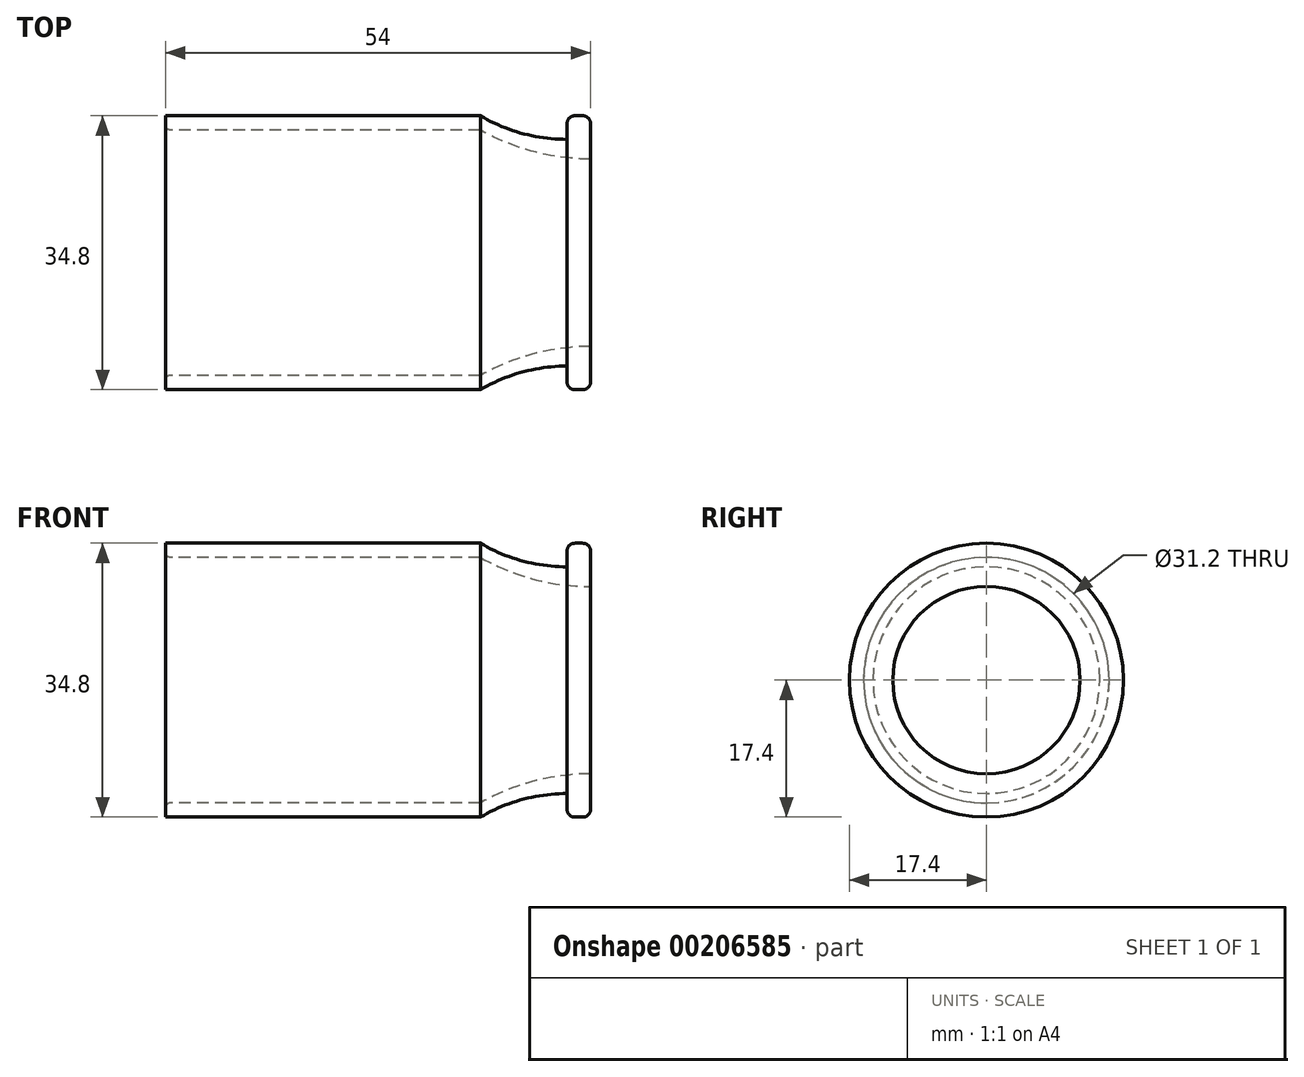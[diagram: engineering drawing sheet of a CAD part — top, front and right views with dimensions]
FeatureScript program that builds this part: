
annotation { "Feature Type Name" : "Feature", "Feature Type Description" : "" }
export const myFeature = defineFeature(function(context is Context, id is Id, definition is map)
    precondition{}
    {
        {
            var Q0;
            Q0=qCreatedBy(makeId("Front.planeOp"),FACE);
            var sketch = newSketch(context, id + "F0", { "sketchPlane" : qUnion([Q0])});
            skLineSegment(sketch, "E0", {"start": v(11.5, 17.4) * mm, "end": v(40, 17.4) * mm});
            skLineSegment(sketch, "E1", {"start": v(54, 17.4) * mm, "end": v(54, 11.9) * mm});
            skLineSegment(sketch, "E2", {"start": v(0, 0) * mm, "end": v(54, 0) * mm, "construction": true});
            skArc(sketch, "E3", {"start": v(40, 17.4) * mm, "mid": v(45.3, 15.16) * mm, "end": v(51, 14.4) * mm});
            skLineSegment(sketch, "E4", {"start": v(51, 14.4) * mm, "end": v(51, 17.4) * mm});
            skLineSegment(sketch, "E5.trimOffspring", {"start": v(51, 17.4) * mm, "end": v(54, 17.4) * mm});
            skLineSegment(sketch, "E6", {"start": v(11.5, 17.4) * mm, "end": v(0, 17.4) * mm});
            skLineSegment(sketch, "E7", {"start": v(0, 17.4) * mm, "end": v(0, 15.6) * mm});
            skLineSegment(sketch, "E8", {"start": v(0, 15.6) * mm, "end": v(40, 15.6) * mm});
            skArc(sketch, "E9", {"start": v(40, 15.6) * mm, "mid": v(46.76, 12.84) * mm, "end": v(54, 11.9) * mm});
            skSolve(sketch);
        }
        {
            var Q0;
            Q0=makeQuery(id+"F0.imprint","IMPRINT",FACE,{"disambiguationData":[TD([[makeQuery(id+"F0.imprint","IMPRINT",EDGE,{"derivedFrom":sQuery(id+"F0.wireOp",EDGE,"E0")}),-1.0]])]});
            var Q1;
            Q1=sQuery(id+"F0.wireOp",EDGE,"E2");
            revolve(context, id + "F1", {"entities" : qUnion([Q0]), "axis" : qUnion([Q1]), "revolveType" : RevolveType.FULL});
        }
        {
            var Q0;
            Q0=makeQuery(id+"F1.opRevolve","SWEPT_EDGE",EDGE,{"disambiguationData":[OSD([sQuery(id+"F0.wireOp",EDGE,"ZSFxASLh-0yP5-p6YM-MmJs-5nR8J76ZsTdp"),sQuery(id+"F0.wireOp",EDGE,"99mCaiaf-f6u9-JBpr-5VTC-9JCxaVtcxBWm")])]});
            var Q1;
            Q1=makeQuery(id+"F1.opRevolve","SWEPT_EDGE",EDGE,{"disambiguationData":[OSD([sQuery(id+"F0.wireOp",EDGE,"E1"),sQuery(id+"F0.wireOp",EDGE,"E5.trimOffspring")])]});
            var Q2;
            Q2=makeQuery(id+"F1.opRevolve","SWEPT_EDGE",EDGE,{"disambiguationData":[OSD([sQuery(id+"F0.wireOp",EDGE,"E4"),sQuery(id+"F0.wireOp",EDGE,"E5.trimOffspring")])]});
            fillet(context, id + "F2", {"entities" : qUnion([Q0, Q1, Q2]), "radius" : 1 * mm, "tangentPropagation" : true, "allowEdgeOverflow" : false});
        }
        {
            var Q0;
            Q0=makeQuery(id+"F1.opRevolve","SWEPT_EDGE",EDGE,{"disambiguationData":[OSD([sQuery(id+"F0.wireOp",EDGE,"E7"),sQuery(id+"F0.wireOp",EDGE,"E8")])]});
            fillet(context, id + "F3", {"entities" : qUnion([Q0]), "radius" : .6 * mm, "tangentPropagation" : true, "allowEdgeOverflow" : false});
        }
    });
